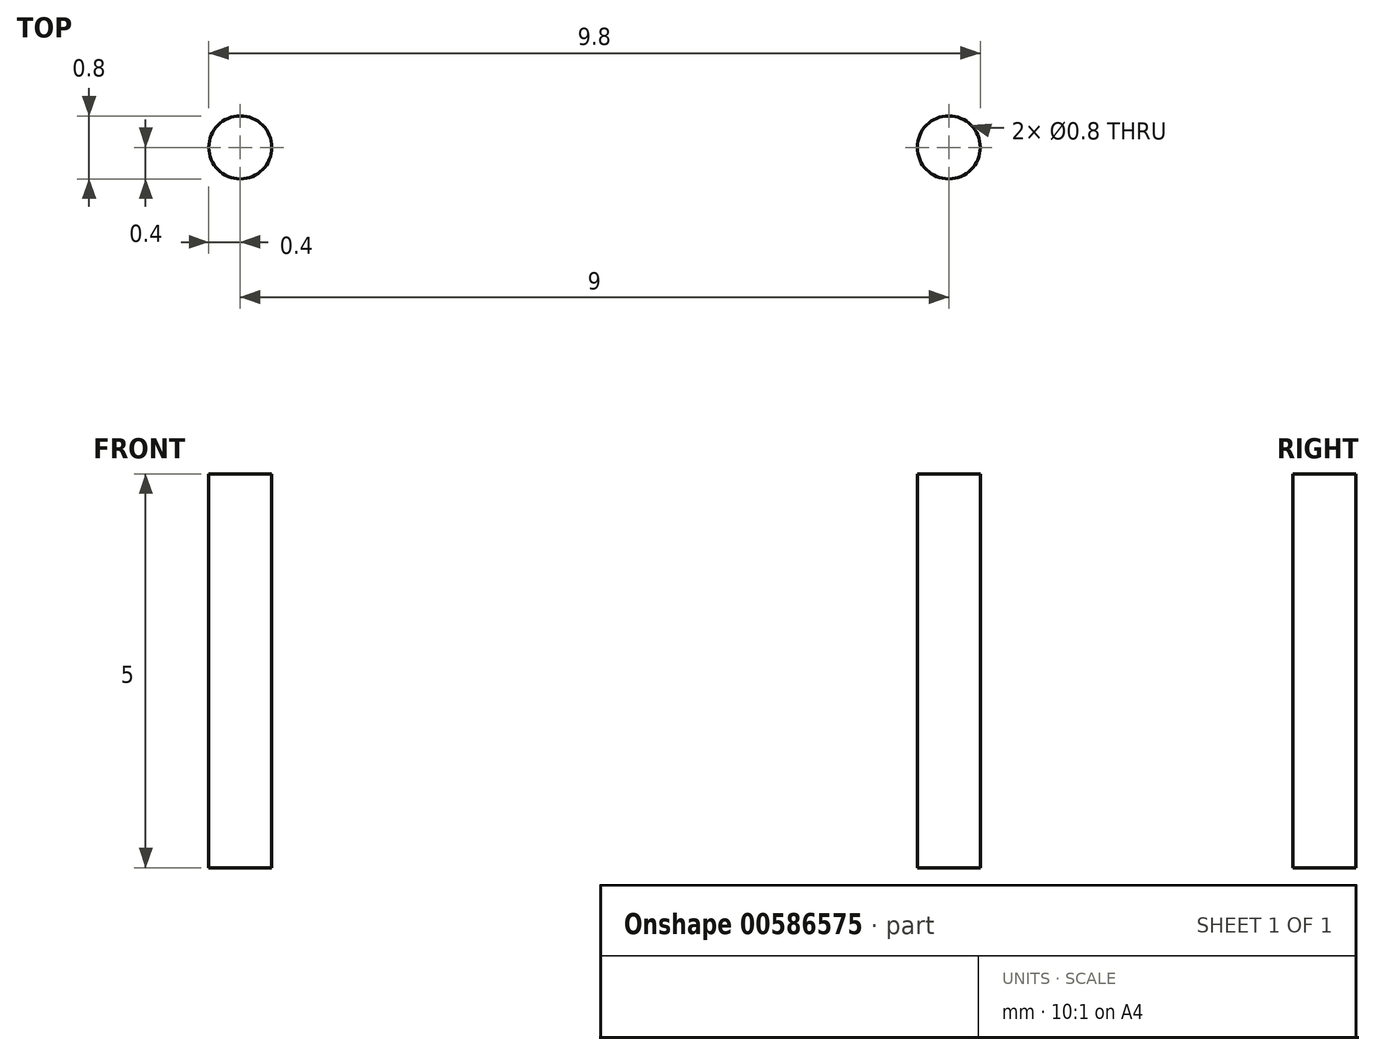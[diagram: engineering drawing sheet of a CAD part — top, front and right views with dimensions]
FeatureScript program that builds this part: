
annotation { "Feature Type Name" : "Feature", "Feature Type Description" : "" }
export const myFeature = defineFeature(function(context is Context, id is Id, definition is map)
    precondition{}
    {
        {
            var Q0;
            Q0=qCreatedBy(makeId("Top.planeOp"),FACE);
            var sketch = newSketch(context, id + "F0", { "sketchPlane" : qUnion([Q0])});
            skLineSegment(sketch, "E0.bottom", {"start": v(7, 2.5) * mm, "end": v(-7, 2.5) * mm});
            skLineSegment(sketch, "E0.top", {"start": v(7, -2.5) * mm, "end": v(-7, -2.5) * mm});
            skLineSegment(sketch, "E0.left", {"start": v(7, 2.5) * mm, "end": v(7, -2.5) * mm});
            skLineSegment(sketch, "E0.right", {"start": v(-7, 2.5) * mm, "end": v(-7, -2.5) * mm});
            skPoint(sketch, "E0.middle", {"position": v(0, 0) * mm});
            skLineSegment(sketch, "E1", {"start": v(-8.3, 0) * mm, "end": v(8.55, 0) * mm, "construction": true});
            skPoint(sketch, "E1.endSnap0", {"position": v(7, 0) * mm});
            skCircle(sketch, "E2", {"center": v(-4.5, 0) * mm, "radius": 0.4 * mm});
            skCircle(sketch, "E3", {"center": v(4.5, 0) * mm, "radius": 0.4 * mm});
            skSolve(sketch);
        }
        {
            var Q0;
            Q0=sQuery(id+"F0.wireOp",EDGE,"E2");
            var Q1;
            Q1=sQuery(id+"F0.wireOp",EDGE,"E3");
            extrude(context, id + "F1", {"bodyType" : ToolBodyType.SURFACE, "surfaceEntities" : qUnion([Q0, Q1]), "depth" : -5 * mm, "offsetDistance" : 25.4 * mm});
        }
    });
